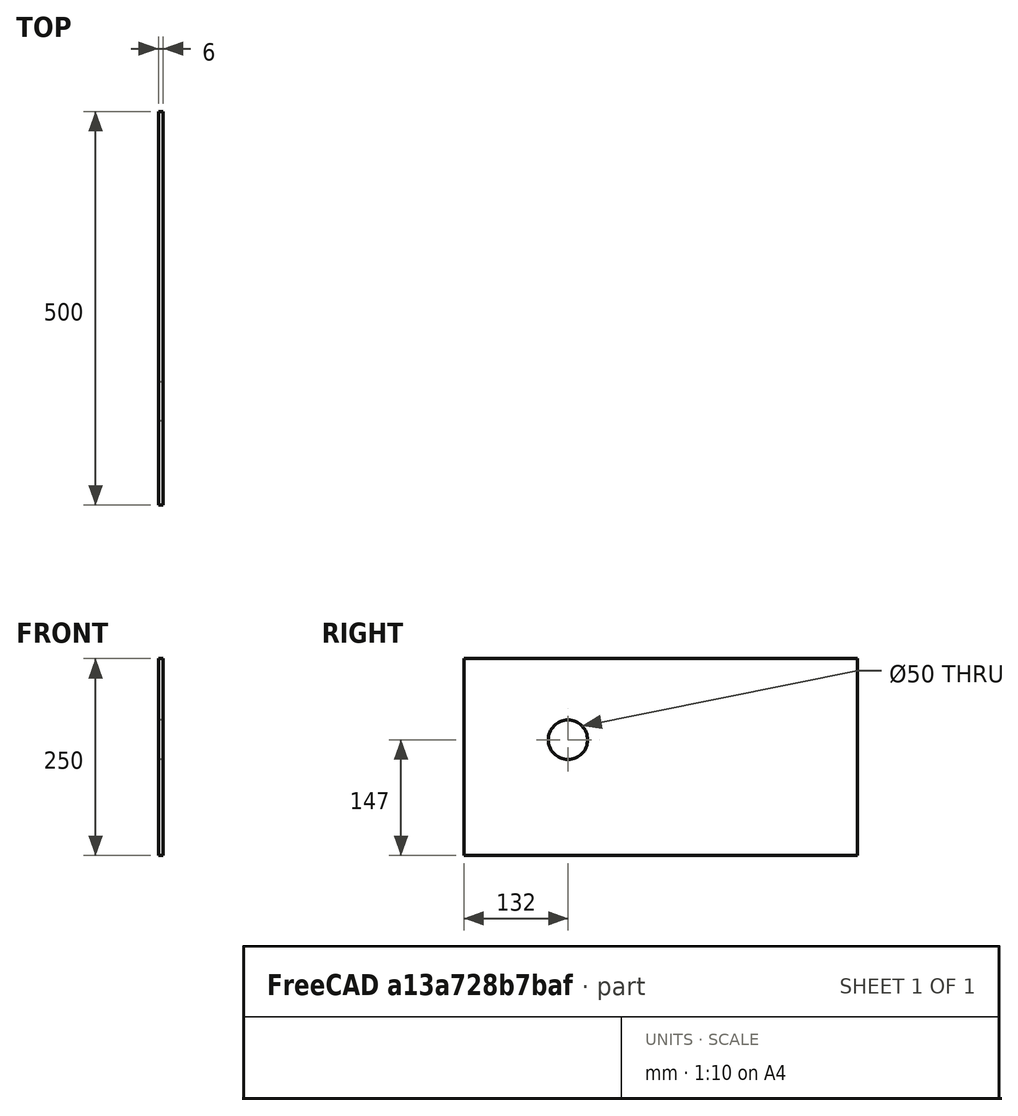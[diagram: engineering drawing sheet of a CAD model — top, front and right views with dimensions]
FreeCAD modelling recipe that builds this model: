
FCSTD DOCUMENT  (FreeCAD 0.18R4 (GitTag))
Label: Gabinete_Lateral1
License: All rights reserved
LicenseURL: http://en.wikipedia.org/wiki/All_rights_reserved
objects: Sketcher::SketchObject×1, PartDesign::Pad×1, PartDesign::Body×1
note: 4 computed .brp shape members not serialized (recipe doc carries the construction recipe); baked Part::Feature solids carry a one-line shape summary decoded from their .brp

FEATURE [Sketcher::SketchObject] Sketch
  MapMode = 5
  Placement = pos=(0,0,0) rot=(0.57735,0.57735,0.57735;2.0944rad)
  Support = -> [YZ_Plane]
  sketch-geometry (5):
    g0: LineSegment StartX=0 StartY=0 StartZ=0 EndX=500 EndY=0 EndZ=0
    g1: LineSegment StartX=500 StartY=0 StartZ=0 EndX=500 EndY=250 EndZ=0
    g2: LineSegment StartX=500 StartY=250 StartZ=0 EndX=0 EndY=250 EndZ=0
    g3: LineSegment StartX=0 StartY=250 StartZ=0 EndX=0 EndY=0 EndZ=0
    g4: Circle CenterX=132 CenterY=147 CenterZ=0 NormalX=0 NormalY=0 NormalZ=1 AngleXU=0 Radius=25
  constraints (14):
    c: Coincident(g0,g1)
    c: Coincident(g1,g2)
    c: Coincident(g2,g3)
    c: Coincident(g3,g0)
    c: Horizontal(g0)
    c: Horizontal(g2)
    c: Vertical(g1)
    c: Vertical(g3)
    c: Coincident(g0,g-1)
    c: DistanceX(g0,g0) = 500
    c: DistanceY(g3,g3) = 250
    c: Radius(g4) = 25
    c: Distance(g4,g0) = 147
    c: Distance(g4,g3) = 132
FEATURE [PartDesign::Pad] Pad
  Length = 6
  Length2 = 100
  Placement = pos=(0,0,0) rot=(0.57735,0.57735,0.57735;2.0944rad)
  Profile = -> Sketch
  Type = 0
FEATURE [PartDesign::Body] Body
  Group = -> [Sketch,Pad]
  Origin = -> Origin
  Tip = -> Pad
